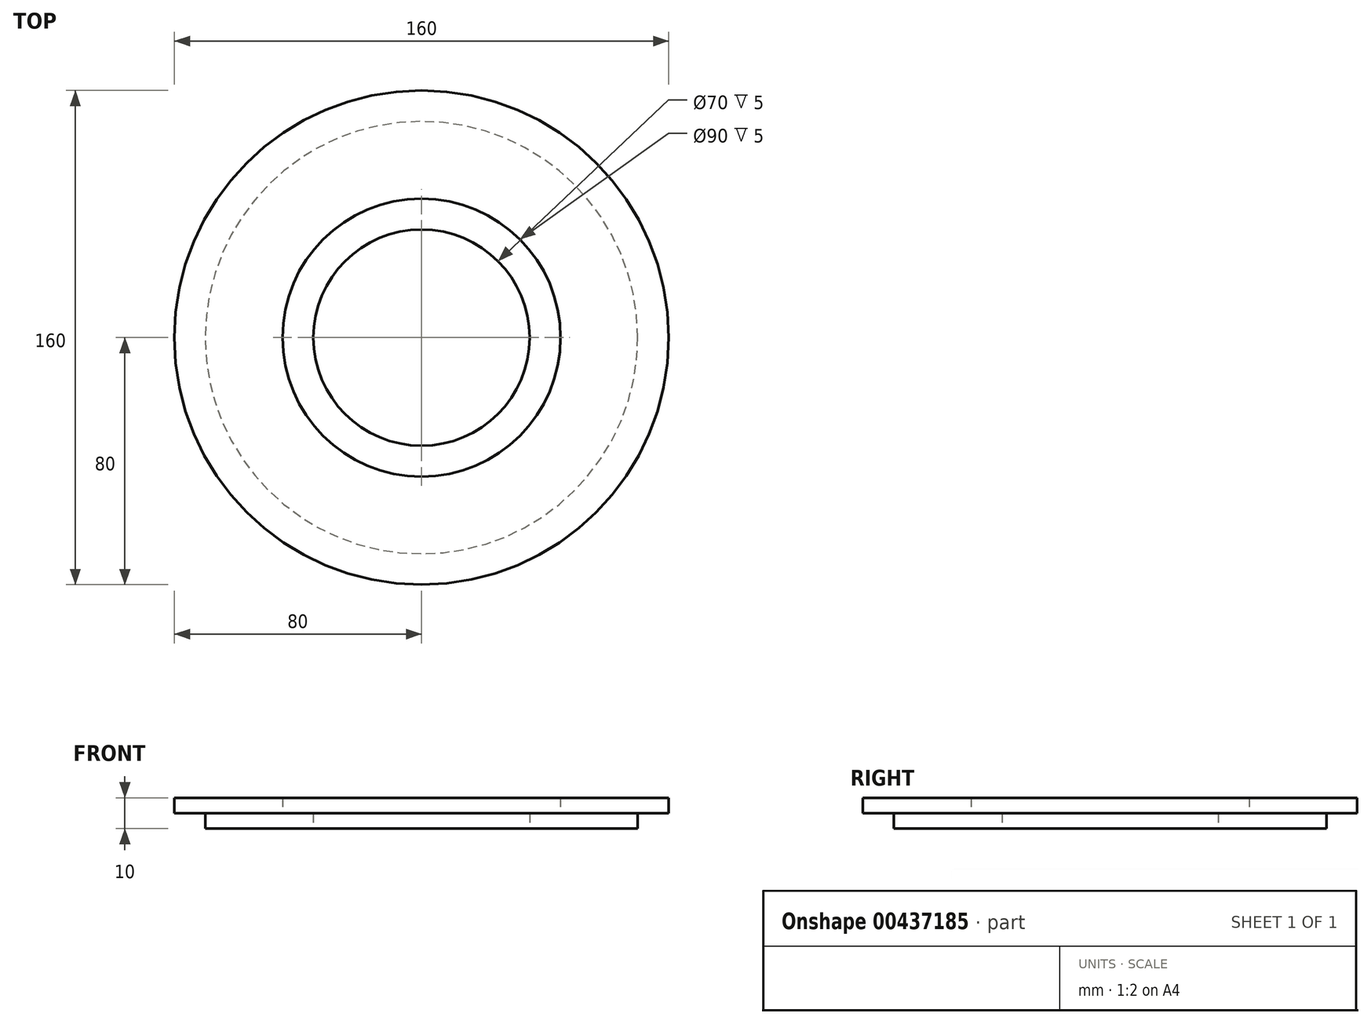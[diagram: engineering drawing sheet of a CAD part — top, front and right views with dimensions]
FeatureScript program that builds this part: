
annotation { "Feature Type Name" : "Feature", "Feature Type Description" : "" }
export const myFeature = defineFeature(function(context is Context, id is Id, definition is map)
    precondition{}
    {
        {
            var Q0;
            Q0=qCreatedBy(makeId("Front.planeOp"),FACE);
            var sketch = newSketch(context, id + "F0", { "sketchPlane" : qUnion([Q0])});
            skLineSegment(sketch, "E0", {"start": v(35, 0) * mm, "end": v(70, 0) * mm});
            skLineSegment(sketch, "E1", {"start": v(70, 0) * mm, "end": v(70, 5) * mm});
            skLineSegment(sketch, "E2", {"start": v(70, 5) * mm, "end": v(80, 5) * mm});
            skLineSegment(sketch, "E3", {"start": v(80, 5) * mm, "end": v(80, 10) * mm});
            skLineSegment(sketch, "E4", {"start": v(80, 10) * mm, "end": v(45, 10) * mm});
            skLineSegment(sketch, "E5", {"start": v(45, 10) * mm, "end": v(45, 5) * mm});
            skLineSegment(sketch, "E6", {"start": v(45, 5) * mm, "end": v(35, 5) * mm});
            skLineSegment(sketch, "E7", {"start": v(35, 5) * mm, "end": v(35, 0) * mm});
            skLineSegment(sketch, "E8", {"start": v(0, 0) * mm, "end": v(0, 115.63) * mm, "construction": true});
            skSolve(sketch);
        }
        {
            var Q0;
            Q0=makeQuery(id+"F0.imprint","IMPRINT",FACE,{"disambiguationData":[TD([[makeQuery(id+"F0.imprint","IMPRINT",EDGE,{"derivedFrom":sQuery(id+"F0.wireOp",EDGE,"E0")}),1.0]])]});
            var Q1;
            Q1=sQuery(id+"F0.wireOp",EDGE,"E8");
            var Q2;
            Q2=sQuery(id+"F0.wireOp",EDGE,"E8");
            revolve(context, id + "F1", {"entities" : qUnion([Q0]), "surfaceEntities" : qUnion([Q1]), "axis" : qUnion([Q2]), "revolveType" : RevolveType.FULL});
        }
    });
